FCSTD DOCUMENT  (FreeCAD 0.19R24291 (Git))
Label: Problem 09
License: All rights reserved
LicenseURL: http://en.wikipedia.org/wiki/All_rights_reserved
objects: Part::Part2DObjectPython×72, App::FeaturePython×42, Part::Mirroring×7
note: 79 computed .brp shape members not serialized (recipe doc carries the construction recipe); baked Part::Feature solids carry a one-line shape summary decoded from their .brp

FEATURE [Part::Part2DObjectPython] Line  # Draft 2D object (typed FeaturePython)
  Area = 0
  ChamferSize = 0
  Closed = false
  End = (-88.4143,-6.28415,0)
  FilletRadius = 0
  Length = 66.1082
  MakeFace = false
  Placement = pos=(-8.14865,-6.28415,0) rot=(0,0,1;0rad)
  Points = (2) [(-14.1575,6.21725e-15,0),(-80.2657,-8.88178e-16,0)]
  Start = (-22.3061,-6.28415,0)
  Subdivisions = 0
FEATURE [Part::Part2DObjectPython] Circle  # Draft 2D object (typed FeaturePython)
  Area = 0
  FirstAngle = 0
  LastAngle = 0
  MakeFace = false
  Placement = pos=(-1.0929,-49.8088,0) rot=(0,0,1;0rad)
  Radius = 30
FEATURE [Part::Part2DObjectPython] Line001  # Draft 2D object (typed FeaturePython)
  Area = 0
  ChamferSize = 0
  Closed = false
  End = (-31.0929,-6.28415,0)
  FilletRadius = 0
  Length = 43.5246
  MakeFace = false
  Placement = pos=(-31.0929,-49.8088,0) rot=(0,0,1;0rad)
  Points = (2) [(-7.10543e-15,1.13687e-13,0),(-3.55271e-15,43.5246,0)]
  Start = (-31.0929,-49.8088,0)
  Subdivisions = 0
FEATURE [Part::Part2DObjectPython] Line002  # Draft 2D object (typed FeaturePython)
  Area = 0
  ChamferSize = 0
  Closed = false
  End = (28.9071,-6.28415,0)
  FilletRadius = 0
  Length = 43.5246
  MakeFace = false
  Placement = pos=(28.9071,-49.8088,0) rot=(0,0,1;0rad)
  Points = (2) [(0,0,0),(3.55271e-15,43.5246,0)]
  Start = (28.9071,-49.8088,0)
  Subdivisions = 0
FEATURE [Part::Part2DObjectPython] Line003  # Draft 2D object (typed FeaturePython)
  Area = 0
  ChamferSize = 0
  Closed = false
  End = (-31.061,13.6349,0)
  FilletRadius = 0
  Length = 19.9191
  MakeFace = false
  Placement = pos=(-31.0929,-6.28415,0) rot=(0,0,-1;1.33891rad)
  Points = (2) [(0,0,0),(-19.3786,4.60874,0)]
  Start = (-31.0929,-6.28415,0)
  Subdivisions = 0
FEATURE [Part::Part2DObjectPython] Line004  # Draft 2D object (typed FeaturePython)
  Area = 0
  ChamferSize = 0
  Closed = false
  End = (28.9071,-6.28415,0)
  FilletRadius = 0
  Length = 60
  MakeFace = false
  Placement = pos=(-31.0929,-6.28415,0) rot=(0,0,1;0rad)
  Points = (2) [(0,0,0),(60,-8.88178e-15,0)]
  Start = (-31.0929,-6.28415,0)
  Subdivisions = 0
FEATURE [Part::Part2DObjectPython] Line005  # Draft 2D object (typed FeaturePython)
  Area = 0
  ChamferSize = 0
  Closed = false
  End = (28.9071,73.7165,0)
  FilletRadius = 0
  Length = 60
  MakeFace = false
  Points = (2) [(-31.0929,73.7165,0),(28.9071,73.7165,0)]
  Start = (-31.0929,73.7165,0)
  Subdivisions = 0
FEATURE [Part::Part2DObjectPython] Line006  # Draft 2D object (typed FeaturePython)
  Area = 0
  ChamferSize = 0
  Closed = false
  End = (28.9757,54.2966,0)
  FilletRadius = 0
  Length = 19.4201
  MakeFace = false
  Placement = pos=(28.9071,73.7165,0) rot=(0,0,1;0rad)
  Points = (2) [(0,0,0),(0.0686363,-19.4199,0)]
  Start = (28.9071,73.7165,0)
  Subdivisions = 0
FEATURE [Part::Part2DObjectPython] Line007  # Draft 2D object (typed FeaturePython)
  Area = 0
  ChamferSize = 0
  Closed = false
  End = (142.077,-19.8088,0)
  FilletRadius = 0
  Length = 143.169
  MakeFace = false
  Points = (2) [(-1.0929,-19.8088,0),(142.077,-19.8088,0)]
  Start = (-1.0929,-19.8088,0)
  Subdivisions = 0
FEATURE [Part::Part2DObjectPython] Line008  # Draft 2D object (typed FeaturePython)
  Area = 0
  ChamferSize = 0
  Closed = false
  End = (-1.0929,-79.8088,0)
  FilletRadius = 0
  Length = 203.169
  MakeFace = false
  Points = (2) [(202.077,-79.8088,0),(-1.0929,-79.8088,0)]
  Start = (202.077,-79.8088,0)
  Subdivisions = 0
FEATURE [Part::Part2DObjectPython] Line010  # Draft 2D object (typed FeaturePython)
  Area = 0
  ChamferSize = 0
  Closed = false
  End = (142.077,73.7158,0)
  FilletRadius = 0
  Length = 80
  MakeFace = false
  Placement = pos=(142.077,-19.8088,0) rot=(0,0,1;0rad)
  Points = (2) [(0,13.5246,0),(0,93.5246,0)]
  Start = (142.077,-6.28415,0)
  Subdivisions = 0
FEATURE [Part::Part2DObjectPython] Line011  # Draft 2D object (typed FeaturePython)
  Area = 0
  ChamferSize = 0
  Closed = false
  End = (202.077,73.7158,0)
  FilletRadius = 0
  Length = 80
  MakeFace = false
  Placement = pos=(202.077,-79.8088,0) rot=(0,0,1;0rad)
  Points = (2) [(0,73.5246,0),(-2.84217e-14,153.525,0)]
  Start = (202.077,-6.28415,0)
  Subdivisions = 0
FEATURE [Part::Part2DObjectPython] Line012  # Draft 2D object (typed FeaturePython)
  Area = 0
  ChamferSize = 0
  Closed = false
  End = (142.077,-6.28415,0)
  FilletRadius = 0
  Length = 73.5246
  MakeFace = false
  Placement = pos=(142.077,-19.8088,0) rot=(0,0,1;0rad)
  Points = (2) [(0,-60,0),(0,13.5246,0)]
  Start = (142.077,-79.8088,0)
  Subdivisions = 0
FEATURE [Part::Part2DObjectPython] Line013  # Draft 2D object (typed FeaturePython)
  Area = 0
  ChamferSize = 0
  Closed = false
  End = (202.077,-6.28415,0)
  FilletRadius = 0
  Length = 73.5246
  MakeFace = false
  Placement = pos=(202.077,-79.8088,0) rot=(0,0,1;0rad)
  Points = (2) [(0,0,0),(0,73.5246,0)]
  Start = (202.077,-79.8088,0)
  Subdivisions = 0
FEATURE [Part::Part2DObjectPython] Line014  # Draft 2D object (typed FeaturePython)
  Area = 0
  ChamferSize = 0
  Closed = false
  End = (202.077,73.7158,0)
  FilletRadius = 0
  Length = 60
  MakeFace = false
  Placement = pos=(142.077,73.7158,0) rot=(0,0,1;0rad)
  Points = (2) [(0,0,0),(60,1.42109e-14,0)]
  Start = (142.077,73.7158,0)
  Subdivisions = 0
FEATURE [Part::Part2DObjectPython] Line015  # Draft 2D object (typed FeaturePython)
  Area = 0
  ChamferSize = 0
  Closed = false
  End = (172.077,73.7158,0)
  FilletRadius = 0
  Length = 123.525
  MakeFace = false
  Placement = pos=(172.077,73.7158,0) rot=(0,0,1;0rad)
  Points = (2) [(0,-123.525,0),(0,0,0)]
  Start = (172.077,-49.8088,0)
  Subdivisions = 0
FEATURE [Part::Part2DObjectPython] Line016  # Draft 2D object (typed FeaturePython)
  Area = 0
  ChamferSize = 0
  Closed = false
  End = (142.077,33.7158,0)
  FilletRadius = 0
  Length = 60
  MakeFace = false
  Placement = pos=(202.077,33.7158,0) rot=(0,0,1;0rad)
  Points = (2) [(0,0,0),(-60,-7.10543e-15,0)]
  Start = (202.077,33.7158,0)
  Subdivisions = 0
FEATURE [Part::Part2DObjectPython] Polygon  # Draft 2D object (typed FeaturePython)
  Area = 0
  ChamferSize = 0
  DrawMode = 0
  FacesNumber = 4
  FilletRadius = 0
  MakeFace = false
  Placement = pos=(172.077,33.7158,0) rot=(0,0,1;0rad)
  Radius = 21.2132
FEATURE [Part::Part2DObjectPython] Line017  # Draft 2D object (typed FeaturePython)
  Area = 0
  ChamferSize = 0
  Closed = false
  End = (150.863,33.7158,0)
  FilletRadius = 0
  Length = 113.525
  MakeFace = false
  Placement = pos=(150.863,33.7158,0) rot=(0,0,1;0rad)
  Points = (2) [(0,-113.525,0),(0,0,0)]
  Start = (150.863,-79.8088,0)
  Subdivisions = 0
FEATURE [Part::Part2DObjectPython] Line018  # Draft 2D object (typed FeaturePython)
  Area = 0
  ChamferSize = 0
  Closed = false
  End = (193.29,33.7158,0)
  FilletRadius = 0
  Length = 113.525
  MakeFace = false
  Placement = pos=(193.29,33.7158,0) rot=(0,0,1;0rad)
  Points = (2) [(0,-113.525,0),(0,0,0)]
  Start = (193.29,-79.8088,0)
  Subdivisions = 0
FEATURE [Part::Part2DObjectPython] Line019  # Draft 2D object (typed FeaturePython)
  Area = 0
  ChamferSize = 0
  Closed = false
  End = (161.47,44.3224,0)
  FilletRadius = 0
  Length = 124.131
  MakeFace = false
  Placement = pos=(161.47,44.3224,0) rot=(0,0,1;0rad)
  Points = (2) [(0,-124.131,0),(0,2.84217e-14,0)]
  Start = (161.47,-79.8088,0)
  Subdivisions = 0
FEATURE [Part::Part2DObjectPython] Line020  # Draft 2D object (typed FeaturePython)
  Area = 0
  ChamferSize = 0
  Closed = false
  End = (182.683,44.3224,0)
  FilletRadius = 0
  Length = 124.131
  MakeFace = false
  Placement = pos=(182.683,44.3224,0) rot=(0,0,1;0rad)
  Points = (2) [(0,-124.131,0),(0,2.84217e-14,0)]
  Start = (182.683,-79.8088,0)
  Subdivisions = 0
FEATURE [App::FeaturePython] Text  # WARN: FeaturePython — macro-defined, semantics opaque (R4)
  Placement = pos=(174.82,55.4955,0) rot=(0,0,1;0rad)
  Text = 1''
FEATURE [App::FeaturePython] Text001  # WARN: FeaturePython — macro-defined, semantics opaque (R4)
  Placement = pos=(183.942,45.1583,0) rot=(0,0,1;0rad)
  Text = 2''
FEATURE [App::FeaturePython] Text002  # WARN: FeaturePython — macro-defined, semantics opaque (R4)
  Placement = pos=(193.671,34.517,0) rot=(0,0,1;0rad)
  Text = 3''
FEATURE [App::FeaturePython] Text003  # WARN: FeaturePython — macro-defined, semantics opaque (R4)
  Placement = pos=(183.942,20.8354,0) rot=(0,0,1;0rad)
  Text = 4''
FEATURE [App::FeaturePython] Text004  # WARN: FeaturePython — macro-defined, semantics opaque (R4)
  Placement = pos=(172.692,8.67401,0) rot=(0,0,1;0rad)
  Text = 5''
FEATURE [App::FeaturePython] Text005  # WARN: FeaturePython — macro-defined, semantics opaque (R4)
  Placement = pos=(156.274,19.0112,0) rot=(0,0,1;0rad)
  Text = 6''
FEATURE [App::FeaturePython] Text006  # WARN: FeaturePython — macro-defined, semantics opaque (R4)
  Placement = pos=(147.457,35.7332,0) rot=(0,0,1;0rad)
  Text = 7''
FEATURE [App::FeaturePython] Text007  # WARN: FeaturePython — macro-defined, semantics opaque (R4)
  Placement = pos=(158.099,43.9421,0) rot=(0,0,1;0rad)
  Text = 8''
FEATURE [Part::Part2DObjectPython] Line022  # Draft 2D object (typed FeaturePython)
  Area = 0
  ChamferSize = 0
  Closed = false
  End = (161.47,-39.2022,0)
  FilletRadius = 0
  Length = 212.563
  MakeFace = false
  Placement = pos=(161.47,-39.2022,0) rot=(0,0,1;0rad)
  Points = (2) [(-212.563,-7.10543e-15,0),(0,0,0)]
  Start = (-51.0929,-39.2022,0)
  Subdivisions = 0
FEATURE [Part::Part2DObjectPython] Line023  # Draft 2D object (typed FeaturePython)
  Area = 0
  ChamferSize = 0
  Closed = false
  End = (182.683,-60.4154,0)
  FilletRadius = 0
  Length = 233.776
  MakeFace = false
  Placement = pos=(182.683,-60.4154,0) rot=(0,0,1;0rad)
  Points = (2) [(-233.776,0,0),(0,0,0)]
  Start = (-51.0929,-60.4154,0)
  Subdivisions = 0
FEATURE [Part::Part2DObjectPython] Line025  # Draft 2D object (typed FeaturePython)
  Area = 0
  ChamferSize = 0
  Closed = false
  End = (-1.0929,73.7165,0)
  FilletRadius = 0
  Length = 153.525
  MakeFace = false
  Placement = pos=(-1.0929,73.7165,0) rot=(0,0,1;0rad)
  Points = (2) [(-1.82077e-14,-153.525,0),(0,0,0)]
  Start = (-1.0929,-79.8088,0)
  Subdivisions = 0
FEATURE [Part::Part2DObjectPython] Line026  # Draft 2D object (typed FeaturePython)
  Area = 0
  ChamferSize = 0
  Closed = false
  End = (-29.1553,73.7165,0)
  FilletRadius = 0
  Length = 134.132
  MakeFace = false
  Placement = pos=(-29.1553,-39.2022,0) rot=(0,0,1;0rad)
  Points = (2) [(-1.06581e-14,-21.2132,0),(3.55271e-15,112.919,0)]
  Start = (-29.1553,-60.4154,0)
  Subdivisions = 0
FEATURE [Part::Part2DObjectPython] Line027  # Draft 2D object (typed FeaturePython)
  Area = 0
  ChamferSize = 0
  Closed = false
  End = (-22.3061,73.7165,0)
  FilletRadius = 0
  Length = 144.739
  MakeFace = false
  Placement = pos=(-22.3061,-71.022,0) rot=(0,0,1;0rad)
  Points = (2) [(0,0,0),(1.77636e-14,144.739,0)]
  Start = (-22.3061,-71.022,0)
  Subdivisions = 0
FEATURE [Part::Part2DObjectPython] Line028  # Draft 2D object (typed FeaturePython)
  Area = 0
  ChamferSize = 0
  Closed = false
  End = (20.1203,73.7165,0)
  FilletRadius = 0
  Length = 144.739
  MakeFace = false
  Placement = pos=(20.1203,-71.022,0) rot=(0,0,1;0rad)
  Points = (2) [(0,0,0),(2.13163e-14,144.739,0)]
  Start = (20.1203,-71.022,0)
  Subdivisions = 0
FEATURE [Part::Part2DObjectPython] Line029  # Draft 2D object (typed FeaturePython)
  Area = 0
  ChamferSize = 0
  Closed = false
  End = (26.9695,73.7165,0)
  FilletRadius = 0
  Length = 134.132
  MakeFace = false
  Placement = pos=(26.9695,-60.4154,0) rot=(0,0,1;0rad)
  Points = (2) [(0,0,0),(2.13163e-14,134.132,0)]
  Start = (26.9695,-60.4154,0)
  Subdivisions = 0
FEATURE [Part::Part2DObjectPython] Line031  # Draft 2D object (typed FeaturePython)
  Area = 0
  ChamferSize = 0
  Closed = false
  End = (182.683,44.3224,0)
  FilletRadius = 0
  Length = 233.776
  MakeFace = false
  Placement = pos=(182.683,44.3224,0) rot=(0,0,1;0rad)
  Points = (2) [(-233.776,7.10543e-15,0),(0,0,0)]
  Start = (-51.0929,44.3224,0)
  Subdivisions = 0
FEATURE [Part::Part2DObjectPython] Line032  # Draft 2D object (typed FeaturePython)
  Area = 0
  ChamferSize = 0
  Closed = false
  End = (182.683,23.1092,0)
  FilletRadius = 0
  Length = 233.776
  MakeFace = false
  Placement = pos=(182.683,23.1092,0) rot=(0,0,1;0rad)
  Points = (2) [(-233.776,2.4869e-14,0),(0,0,0)]
  Start = (-51.0929,23.1092,0)
  Subdivisions = 0
FEATURE [Part::Part2DObjectPython] Line034  # Draft 2D object (typed FeaturePython)
  Area = 0
  ChamferSize = 0
  Closed = false
  End = (29.1711,55.03,0)
  FilletRadius = 0
  Length = 30.2642
  MakeFace = false
  Placement = pos=(-1.0929,54.929,0) rot=(0,0,1;0rad)
  Points = (2) [(0,0,0),(30.264,0.100964,0)]
  Start = (-1.0929,54.929,0)
  Subdivisions = 0
FEATURE [Part::Part2DObjectPython] Line035  # Draft 2D object (typed FeaturePython)
  Area = 0
  ChamferSize = 0
  Closed = false
  End = (29.2442,12.5661,0)
  FilletRadius = 0
  Length = 30.3372
  MakeFace = false
  Placement = pos=(-1.0929,12.5026,0) rot=(0,0,1;0rad)
  Points = (2) [(0,0,0),(30.3371,0.0634774,0)]
  Start = (-1.0929,12.5026,0)
  Subdivisions = 0
FEATURE [Part::Mirroring] mirror  label="Line034 (mirrored)"
  Base = (-1.0929,73.7165,0)
  Normal = (-1,1e-16,0)
  Source = -> Line034
FEATURE [Part::Mirroring] mirror001  label="Line035 (mirrored)"
  Base = (-1.0929,73.7165,0)
  Normal = (-1,1e-16,0)
  Source = -> Line035
FEATURE [Part::Part2DObjectPython] Line036  # Draft 2D object (typed FeaturePython)
  Area = 0
  ChamferSize = 0
  Closed = false
  End = (48.9071,23.1092,0)
  FilletRadius = 0
  Length = 31.8198
  MakeFace = false
  Placement = pos=(48.9071,54.929,0) rot=(0,0,1;0rad)
  Points = (2) [(0,0,0),(-7.10543e-15,-31.8198,0)]
  Start = (48.9071,54.929,0)
  Subdivisions = 0
FEATURE [Part::Part2DObjectPython] Line037  # Draft 2D object (typed FeaturePython)
  Area = 0
  ChamferSize = 0
  Closed = false
  End = (-51.0929,12.5026,0)
  FilletRadius = 0
  Length = 42.4264
  MakeFace = false
  Placement = pos=(-51.0929,54.929,0) rot=(0,0,1;0rad)
  Points = (2) [(0,0,0),(0,-42.4264,0)]
  Start = (-51.0929,54.929,0)
  Subdivisions = 0
FEATURE [App::FeaturePython] Text008  # WARN: FeaturePython — macro-defined, semantics opaque (R4)
  Placement = pos=(-34.6601,54.8874,0) rot=(0,0,1;0rad)
  Text = 1'
FEATURE [App::FeaturePython] Text009  # WARN: FeaturePython — macro-defined, semantics opaque (R4)
  Placement = pos=(30.4035,55.4955,0) rot=(0,0,1;0rad)
  Text = 1'
FEATURE [App::FeaturePython] Text010  # WARN: FeaturePython — macro-defined, semantics opaque (R4)
  Placement = pos=(-42.565,45.1583,0) rot=(0,0,1;0rad)
  Text = 2'(8')
FEATURE [App::FeaturePython] Text011  # WARN: FeaturePython — macro-defined, semantics opaque (R4)
  Placement = pos=(31.0116,44.8543,0) rot=(0,0,1;0rad)
  Text = 2'(8')
FEATURE [App::FeaturePython] Text012  # WARN: FeaturePython — macro-defined, semantics opaque (R4)
  Placement = pos=(-41.9569,24.4839,0) rot=(0,0,1;0rad)
  Text = 4'(6')
FEATURE [App::FeaturePython] Text013  # WARN: FeaturePython — macro-defined, semantics opaque (R4)
  Placement = pos=(30.7076,23.8758,0) rot=(0,0,1;0rad)
  Text = 4'(6')
FEATURE [App::FeaturePython] Text014  # WARN: FeaturePython — macro-defined, semantics opaque (R4)
  Placement = pos=(-36.1803,6.84981,0) rot=(0,0,1;0rad)
  Text = 5'
FEATURE [App::FeaturePython] Text015  # WARN: FeaturePython — macro-defined, semantics opaque (R4)
  Placement = pos=(31.9237,7.15383,0) rot=(0,0,1;0rad)
  Text = 5'
FEATURE [App::FeaturePython] Text016  # WARN: FeaturePython — macro-defined, semantics opaque (R4)
  Placement = pos=(-36.1803,74.6497,0) rot=(0,0,1;0rad)
  Text = p'
FEATURE [App::FeaturePython] Text017  # WARN: FeaturePython — macro-defined, semantics opaque (R4)
  Placement = pos=(30.4035,74.6497,0) rot=(0,0,1;0rad)
  Text = r'
FEATURE [App::FeaturePython] Text018  # WARN: FeaturePython — macro-defined, semantics opaque (R4)
  Placement = pos=(-35.5722,-5.00759,0) rot=(0,0,1;0rad)
  Text = i'
FEATURE [App::FeaturePython] Text019  # WARN: FeaturePython — macro-defined, semantics opaque (R4)
  Placement = pos=(30.7076,-5.9197,0) rot=(0,0,1;0rad)
  Text = k'
FEATURE [App::FeaturePython] Text020  # WARN: FeaturePython — macro-defined, semantics opaque (R4)
  Placement = pos=(-7.62939e-06,-5.00759,0) rot=(0,0,1;0rad)
  Text = j'(l')
FEATURE [App::FeaturePython] Text021  # WARN: FeaturePython — macro-defined, semantics opaque (R4)
  Placement = pos=(-3.64843,76.1699,0) rot=(0,0,1;0rad)
  Text = q'(s')
FEATURE [App::FeaturePython] Text022  # WARN: FeaturePython — macro-defined, semantics opaque (R4)
  Placement = pos=(-0.608087,-18.6892,0) rot=(0,0,1;0rad)
  Text = s(l)
FEATURE [App::FeaturePython] Text023  # WARN: FeaturePython — macro-defined, semantics opaque (R4)
  Placement = pos=(-38.6125,-56.3896,0) rot=(0,0,1;0rad)
  Text = p(i)
FEATURE [App::FeaturePython] Text024  # WARN: FeaturePython — macro-defined, semantics opaque (R4)
  Placement = pos=(30.7076,-56.3896,0) rot=(0,0,1;0rad)
  Text = r(k)
FEATURE [App::FeaturePython] Text025  # WARN: FeaturePython — macro-defined, semantics opaque (R4)
  Placement = pos=(-3.04037,-86.4891,0) rot=(0,0,1;0rad)
  Text = q(j)
FEATURE [Part::Part2DObjectPython] BSpline  # Draft 2D object (typed FeaturePython)
  Area = 0
  Closed = false
  MakeFace = false
  Parameterization = 1
  Points = (3) [(28.9071,54.929,0),(26.9695,44.3224,0),(20.1203,33.7158,0)]
FEATURE [Part::Mirroring] mirror002  label="BSpline (mirrored)"
  Base = (-1.0929,54.929,0)
  Normal = (-1,-4e-16,0)
  Source = -> BSpline
FEATURE [Part::Mirroring] mirror003  label="BSpline (mirrored) (mirrored)"
  Base = (-31.0288,33.7158,0)
  Normal = (0,-1,0)
  Source = -> mirror002
FEATURE [Part::Mirroring] mirror004  label="BSpline (mirrored)001"
  Base = (-31.0288,33.7158,0)
  Normal = (0,-1,0)
  Source = -> BSpline
FEATURE [Part::Part2DObjectPython] Line039  # Draft 2D object (typed FeaturePython)
  Area = 0
  ChamferSize = 0
  Closed = false
  End = (48.9071,-28.5956,0)
  FilletRadius = 0
  Length = 28.7868
  MakeFace = false
  Points = (2) [(20.1203,-28.5956,0),(48.9071,-28.5956,0)]
  Start = (20.1203,-28.5956,0)
  Subdivisions = 0
FEATURE [Part::Part2DObjectPython] Line040  # Draft 2D object (typed FeaturePython)
  Area = 0
  ChamferSize = 0
  Closed = false
  End = (-51.0929,-28.5956,0)
  FilletRadius = 0
  Length = 28.7868
  MakeFace = false
  Points = (2) [(-22.3061,-28.5956,0),(-51.0929,-28.5956,0)]
  Start = (-22.3061,-28.5956,0)
  Subdivisions = 0
FEATURE [Part::Mirroring] mirror005  label="Line039 (mirrored)"
  Base = (-1.0929,-49.8088,0)
  Normal = (0,1,0)
  Source = -> Line039
FEATURE [Part::Mirroring] mirror006  label="Line040 (mirrored)"
  Base = (-1.0929,-49.8088,0)
  Normal = (0,1,0)
  Source = -> Line040
FEATURE [Part::Part2DObjectPython] Line041  # Draft 2D object (typed FeaturePython)
  Area = 0
  ChamferSize = 0
  Closed = false
  End = (48.9071,-71.022,0)
  FilletRadius = 0
  Length = 42.4264
  MakeFace = false
  Placement = pos=(48.9071,-28.5956,0) rot=(0,0,1;0rad)
  Points = (2) [(0,0,0),(0,-42.4264,0)]
  Start = (48.9071,-28.5956,0)
  Subdivisions = 0
FEATURE [Part::Part2DObjectPython] Line042  # Draft 2D object (typed FeaturePython)
  Area = 0
  ChamferSize = 0
  Closed = false
  End = (-51.0929,-49.8088,0)
  FilletRadius = 0
  Length = 21.2132
  MakeFace = false
  Placement = pos=(-51.0929,-28.5956,0) rot=(0,0,1;0rad)
  Points = (2) [(0,0,0),(0,-21.2132,0)]
  Start = (-51.0929,-28.5956,0)
  Subdivisions = 0
FEATURE [Part::Part2DObjectPython] Line043  # Draft 2D object (typed FeaturePython)
  Area = 0
  ChamferSize = 0
  Closed = false
  End = (20.1203,-28.5956,0)
  FilletRadius = 0
  Length = 42.4264
  MakeFace = false
  Placement = pos=(-22.3061,-28.5956,0) rot=(0,0,1;0rad)
  Points = (2) [(0,0,0),(42.4264,7.10543e-15,0)]
  Start = (-22.3061,-28.5956,0)
  Subdivisions = 0
FEATURE [Part::Part2DObjectPython] Line044  # Draft 2D object (typed FeaturePython)
  Area = 0
  ChamferSize = 0
  Closed = false
  End = (20.1203,-71.022,0)
  FilletRadius = 0
  Length = 42.4264
  MakeFace = false
  Placement = pos=(-22.3061,-71.022,0) rot=(0,0,1;0rad)
  Points = (2) [(0,0,0),(42.4264,0,0)]
  Start = (-22.3061,-71.022,0)
  Subdivisions = 0
FEATURE [App::FeaturePython] Text026  # WARN: FeaturePython — macro-defined, semantics opaque (R4)
  Placement = pos=(-21.5361,28.4601,0) rot=(0,0,1;0rad)
  Text = 3'(7')
FEATURE [App::FeaturePython] Text027  # WARN: FeaturePython — macro-defined, semantics opaque (R4)
  Placement = pos=(7.49369,28.1698,0) rot=(0,0,1;0rad)
  Text = 3'(7')
FEATURE [Part::Part2DObjectPython] Line046  # Draft 2D object (typed FeaturePython)
  Area = 0
  ChamferSize = 0
  Closed = false
  End = (28.9071,-6.28415,0)
  FilletRadius = 0
  Length = 18.1974
  MakeFace = false
  Placement = pos=(28.9071,73.7165,0) rot=(0,0,1;0rad)
  Points = (2) [(0.0686363,-61.8034,0),(1.42109e-14,-80.0007,0)]
  Start = (28.9757,11.9131,0)
  Subdivisions = 0
FEATURE [Part::Part2DObjectPython] Line047  # Draft 2D object (typed FeaturePython)
  Area = 0
  ChamferSize = 0
  Closed = false
  End = (48.9071,54.929,0)
  FilletRadius = 0
  Length = 19.7362
  MakeFace = false
  Placement = pos=(-1.0929,54.929,0) rot=(0,0,1;0rad)
  Points = (2) [(30.264,0.100964,0),(50,-7.10543e-15,0)]
  Start = (29.1711,55.03,0)
  Subdivisions = 0
FEATURE [Part::Part2DObjectPython] Line048  # Draft 2D object (typed FeaturePython)
  Area = 0
  ChamferSize = 0
  Closed = false
  End = (48.9071,12.5026,0)
  FilletRadius = 0
  Length = 19.663
  MakeFace = false
  Placement = pos=(-1.0929,12.5026,0) rot=(0,0,1;0rad)
  Points = (2) [(30.3371,0.0634774,0),(50,-5.32907e-15,0)]
  Start = (29.2442,12.5661,0)
  Subdivisions = 0
FEATURE [Part::Part2DObjectPython] Line049  # Draft 2D object (typed FeaturePython)
  Area = 0
  ChamferSize = 0
  Closed = false
  End = (-31.3569,55.03,0)
  FilletRadius = 0
  Length = 19.7362
  MakeFace = false
  Placement = pos=(-51.0929,54.929,0) rot=(0,0,1;0rad)
  Points = (2) [(0,0,0),(19.736,0.100964,0)]
  Start = (-51.0929,54.929,0)
  Subdivisions = 0
FEATURE [Part::Part2DObjectPython] Line050  # Draft 2D object (typed FeaturePython)
  Area = 0
  ChamferSize = 0
  Closed = false
  End = (-31.43,12.5661,0)
  FilletRadius = 0
  Length = 19.663
  MakeFace = false
  Placement = pos=(-51.0929,12.5026,0) rot=(0,0,1;0rad)
  Points = (2) [(0,0,0),(19.6629,0.0634774,0)]
  Start = (-51.0929,12.5026,0)
  Subdivisions = 0
FEATURE [Part::Part2DObjectPython] Line051  # Draft 2D object (typed FeaturePython)
  Area = 0
  ChamferSize = 0
  Closed = true
  End = (-31.0929,-6.28415,0)
  FilletRadius = 0
  Length = 0
  MakeFace = false
  Placement = pos=(-31.0929,-49.8088,0) rot=(0,0,1;0rad)
  Points = (2) [(-3.55271e-15,43.5246,0),(-3.55271e-15,43.5246,0)]
  Start = (-31.0929,-6.28415,0)
  Subdivisions = 0
FEATURE [Part::Part2DObjectPython] Line052  # Draft 2D object (typed FeaturePython)
  Area = 0
  ChamferSize = 0
  Closed = false
  End = (28.9071,-6.28415,0)
  FilletRadius = 0
  Length = 60
  MakeFace = false
  Placement = pos=(-71.4481,-6.28415,0) rot=(0,0,1;0rad)
  Points = (2) [(40.3552,3.55271e-15,0),(100.355,1.77636e-15,0)]
  Start = (-31.0929,-6.28415,0)
  Subdivisions = 0
FEATURE [Part::Part2DObjectPython] Line053  # Draft 2D object (typed FeaturePython)
  Area = 0
  ChamferSize = 0
  Closed = false
  End = (142.077,-6.28415,0)
  FilletRadius = 0
  Length = 113.169
  MakeFace = false
  Placement = pos=(-71.4481,-6.28415,0) rot=(0,0,1;0rad)
  Points = (2) [(100.355,1.77636e-15,0),(213.525,5.32907e-15,0)]
  Start = (28.9071,-6.28415,0)
  Subdivisions = 0
FEATURE [Part::Part2DObjectPython] Line054  # Draft 2D object (typed FeaturePython)
  Area = 0
  ChamferSize = 0
  Closed = false
  End = (142.077,-6.28415,0)
  FilletRadius = 0
  Length = 0
  MakeFace = false
  Placement = pos=(142.077,-19.8088,0) rot=(0,0,1;0rad)
  Points = (2) [(0,13.5246,0),(0,13.5246,0)]
  Start = (142.077,-6.28415,0)
  Subdivisions = 0
FEATURE [Part::Part2DObjectPython] Line055  # Draft 2D object (typed FeaturePython)
  Area = 0
  ChamferSize = 0
  Closed = false
  End = (202.077,-6.28415,0)
  FilletRadius = 0
  Length = 60
  MakeFace = false
  Placement = pos=(-71.4481,-6.28415,0) rot=(0,0,1;0rad)
  Points = (2) [(213.525,5.32907e-15,0),(273.525,1.06581e-14,0)]
  Start = (142.077,-6.28415,0)
  Subdivisions = 0
FEATURE [Part::Part2DObjectPython] Line056  # Draft 2D object (typed FeaturePython)
  Area = 0
  ChamferSize = 0
  Closed = false
  End = (202.077,-6.28415,0)
  FilletRadius = 0
  Length = 51.2433
  MakeFace = false
  Placement = pos=(-71.4481,-6.28415,0) rot=(0,0,1;0rad)
  Points = (2) [(324.768,1.5099e-14,0),(273.525,1.06581e-14,0)]
  Start = (253.32,-6.28415,0)
  Subdivisions = 0
FEATURE [Part::Part2DObjectPython] Line058  # Draft 2D object (typed FeaturePython)
  Area = 0
  ChamferSize = 0
  Closed = false
  End = (172.077,-49.8088,0)
  FilletRadius = 0
  Length = 123.169
  MakeFace = false
  Placement = pos=(172.077,-49.8088,0) rot=(0,0,1;0rad)
  Points = (2) [(-123.169,2.13163e-14,0),(0,0,0)]
  Start = (48.9071,-49.8088,0)
  Subdivisions = 0
FEATURE [Part::Part2DObjectPython] Line059  # Draft 2D object (typed FeaturePython)
  Area = 0
  ChamferSize = 0
  Closed = false
  End = (28.9071,-49.8088,0)
  FilletRadius = 0
  Length = 60
  MakeFace = false
  Placement = pos=(172.077,-49.8088,0) rot=(0,0,1;0rad)
  Points = (2) [(-203.169,2.84217e-14,0),(-143.169,-7.81597e-14,0)]
  Start = (-31.0929,-49.8088,0)
  Subdivisions = 0
FEATURE [Part::Part2DObjectPython] Line060  # Draft 2D object (typed FeaturePython)
  Area = 0
  ChamferSize = 0
  Closed = false
  End = (-51.0929,-71.022,0)
  FilletRadius = 0
  Length = 21.2132
  MakeFace = false
  Placement = pos=(-51.0929,-28.5956,0) rot=(0,0,1;0rad)
  Points = (2) [(0,-21.2132,0),(0,-42.4264,0)]
  Start = (-51.0929,-49.8088,0)
  Subdivisions = 0
FEATURE [Part::Part2DObjectPython] Line061  # Draft 2D object (typed FeaturePython)
  Area = 0
  ChamferSize = 0
  Closed = false
  End = (-31.0929,-49.8088,0)
  FilletRadius = 0
  Length = 20
  MakeFace = false
  Placement = pos=(172.077,-49.8088,0) rot=(0,0,1;0rad)
  Points = (2) [(-223.169,2.84217e-14,0),(-203.169,2.84217e-14,0)]
  Start = (-51.0929,-49.8088,0)
  Subdivisions = 0
FEATURE [Part::Part2DObjectPython] Line062  # Draft 2D object (typed FeaturePython)
  Area = 0
  ChamferSize = 0
  Closed = false
  End = (48.9071,12.5026,0)
  FilletRadius = 0
  Length = 10.6066
  MakeFace = false
  Placement = pos=(48.9071,54.929,0) rot=(0,0,1;0rad)
  Points = (2) [(-7.10543e-15,-31.8198,0),(-7.10543e-15,-42.4264,0)]
  Start = (48.9071,23.1092,0)
  Subdivisions = 0
FEATURE [Part::Part2DObjectPython] Line063  # Draft 2D object (typed FeaturePython)
  Area = 0
  ChamferSize = 0
  Closed = false
  End = (20.1203,33.7158,0)
  FilletRadius = 0
  Length = 42.4264
  MakeFace = false
  Placement = pos=(142.077,33.7158,0) rot=(0,0,1;0rad)
  Points = (2) [(-164.383,2.13163e-14,0),(-121.956,2.13163e-14,0)]
  Start = (-22.3061,33.7158,0)
  Subdivisions = 0
FEATURE [Part::Part2DObjectPython] Line064  # Draft 2D object (typed FeaturePython)
  Area = 0
  ChamferSize = 0
  Closed = false
  End = (48.9071,33.7158,0)
  FilletRadius = 0
  Length = 28.7868
  MakeFace = false
  Placement = pos=(142.077,33.7158,0) rot=(0,0,1;0rad)
  Points = (2) [(-121.956,2.13163e-14,0),(-93.1694,2.84217e-14,0)]
  Start = (20.1203,33.7158,0)
  Subdivisions = 0
FEATURE [Part::Part2DObjectPython] Line065  # Draft 2D object (typed FeaturePython)
  Area = 0
  ChamferSize = 0
  Closed = false
  End = (-30.9646,73.7165,0)
  FilletRadius = 0
  Length = 20.9631
  MakeFace = false
  Placement = pos=(-31.0929,-6.28415,0) rot=(0,0,-1;1.33891rad)
  Points = (2) [(-57.4357,13.6597,0),(-77.83,18.51,0)]
  Start = (-30.9983,52.7535,0)
  Subdivisions = 0
FEATURE [Part::Part2DObjectPython] Line066  # Draft 2D object (typed FeaturePython)
  Area = 0
  ChamferSize = 0
  Closed = false
  End = (28.9757,54.2966,0)
  FilletRadius = 0
  Length = 0
  MakeFace = false
  Placement = pos=(28.9071,73.7165,0) rot=(0,0,1;0rad)
  Points = (2) [(0.0686363,-19.4199,0),(0.0686363,-19.4199,0)]
  Start = (28.9757,54.2966,0)
  Subdivisions = 0
FEATURE [Part::Part2DObjectPython] Line067  # Draft 2D object (typed FeaturePython)
  Area = 0
  ChamferSize = 0
  Closed = false
  End = (-30.9983,52.7535,0)
  FilletRadius = 0
  Length = 39.1186
  MakeFace = false
  Placement = pos=(-31.0929,-6.28415,0) rot=(0,0,-1;1.33891rad)
  Points = (2) [(-19.3786,4.60874,0),(-57.4357,13.6597,0)]
  Start = (-31.061,13.6349,0)
  Subdivisions = 0
FEATURE [Part::Part2DObjectPython] Line068  # Draft 2D object (typed FeaturePython)
  Area = 0
  ChamferSize = 0
  Closed = false
  End = (142.077,33.7158,0)
  FilletRadius = 0
  Length = 93.1694
  MakeFace = false
  Placement = pos=(142.077,33.7158,0) rot=(0,0,1;0rad)
  Points = (2) [(-93.1694,3.55271e-14,0),(0,0,0)]
  Start = (48.9071,33.7158,0)
  Subdivisions = 0
FEATURE [Part::Part2DObjectPython] Line069  # Draft 2D object (typed FeaturePython)
  Area = 0
  ChamferSize = 0
  Closed = false
  End = (-22.3061,33.7158,0)
  FilletRadius = 0
  Length = 28.7868
  MakeFace = false
  Placement = pos=(142.077,33.7158,0) rot=(0,0,1;0rad)
  Points = (2) [(-193.169,2.13163e-14,0),(-164.383,2.13163e-14,0)]
  Start = (-51.0929,33.7158,0)
  Subdivisions = 0
FEATURE [Part::Part2DObjectPython] Line070  # Draft 2D object (typed FeaturePython)
  Area = 0
  ChamferSize = 0
  Closed = false
  End = (28.9071,12.5026,0)
  FilletRadius = 0
  Length = 42.4264
  MakeFace = false
  Placement = pos=(28.9071,54.929,0) rot=(0,0,1;0rad)
  Points = (2) [(0,0,0),(0,-42.4264,0)]
  Start = (28.9071,54.929,0)
  Subdivisions = 0
FEATURE [App::FeaturePython] Dimension  # Draft dimension (typed FeaturePython)
  Diameter = false
  Dimline = (219.292,19.994,0)
  Direction = (0,0,0)
  Distance = 40
  End = (150.863,33.7158,0)
  Normal = (0,0,1)
  Start = (150.863,-6.28415,0)
FEATURE [App::FeaturePython] Dimension001  # Draft dimension (typed FeaturePython)
  Diameter = false
  Dimline = (232.535,-2.66679,0)
  Direction = (0,0,0)
  Distance = 80.0007
  End = (-1.0929,-6.28415,0)
  Normal = (0,0,1)
  Start = (-1.0929,73.7165,0)
FEATURE [Part::Part2DObjectPython] Line009  # Draft 2D object (typed FeaturePython)
  Area = 0
  ChamferSize = 0
  Closed = false
  End = (128.552,-6.28415,0)
  FilletRadius = 0
  Length = 125.763
  MakeFace = false
  Placement = pos=(128.552,-6.28415,0) rot=(0,0,1;0rad)
  Points = (2) [(88.9278,-88.9278,0),(0,1.77636e-15,0)]
  Start = (217.48,-95.212,0)
  Subdivisions = 0
FEATURE [App::FeaturePython] Dimension002  # Draft dimension (typed FeaturePython)
  Angle = 45
  Center = (128.552,-6.28415,0)
  Dimline = (135.708,-11.0699,0)
  FirstAngle = 315
  LastAngle = 360
  Normal = (0,0,1)
FEATURE [Part::Part2DObjectPython] Line071  # Draft 2D object (typed FeaturePython)
  Area = 0
  ChamferSize = 0
  Closed = false
  End = (48.9071,-49.8088,0)
  FilletRadius = 0
  Length = 20
  MakeFace = false
  Placement = pos=(172.077,-49.8088,0) rot=(0,0,1;0rad)
  Points = (2) [(-143.169,-7.81597e-14,0),(-123.169,2.13163e-14,0)]
  Start = (28.9071,-49.8088,0)
  Subdivisions = 0
FEATURE [App::FeaturePython] Dimension003  # Draft dimension (typed FeaturePython)
  Diameter = true
  Dimline = (-29.1553,-39.2022,0)
  Direction = (0,0,0)
  Distance = 60
  End = (-29.1553,-39.2022,0)
  LinkedGeometry = -> [Circle]
  Normal = (0,0,1)
  Start = (26.9695,-60.4154,0)
  Support = -> Circle
FEATURE [Part::Part2DObjectPython] Line072  # Draft 2D object (typed FeaturePython)
  Area = 0
  ChamferSize = 0
  Closed = false
  End = (193.29,-71.022,0)
  FilletRadius = 0
  Length = 144.383
  MakeFace = false
  Placement = pos=(48.9071,-71.022,0) rot=(0,0,1;0rad)
  Points = (2) [(0,0,0),(144.383,-4.26326e-14,0)]
  Start = (48.9071,-71.022,0)
  Subdivisions = 0
FEATURE [Part::Part2DObjectPython] Line073  # Draft 2D object (typed FeaturePython)
  Area = 0
  ChamferSize = 0
  Closed = false
  End = (150.863,-28.5956,0)
  FilletRadius = 0
  Length = 101.956
  MakeFace = false
  Placement = pos=(48.9071,-28.5956,0) rot=(0,0,1;0rad)
  Points = (2) [(0,0,0),(101.956,-3.55271e-15,0)]
  Start = (48.9071,-28.5956,0)
  Subdivisions = 0
FEATURE [Part::Part2DObjectPython] Line074  # Draft 2D object (typed FeaturePython)
  Area = 0
  ChamferSize = 0
  Closed = false
  End = (172.077,54.929,0)
  FilletRadius = 0
  Length = 123.169
  MakeFace = false
  Placement = pos=(48.9071,54.929,0) rot=(0,0,1;0rad)
  Points = (2) [(0,0,0),(123.169,-1.42109e-14,0)]
  Start = (48.9071,54.929,0)
  Subdivisions = 0
FEATURE [Part::Part2DObjectPython] Line075  # Draft 2D object (typed FeaturePython)
  Area = 0
  ChamferSize = 0
  Closed = false
  End = (172.077,12.5026,0)
  FilletRadius = 0
  Length = 123.169
  MakeFace = false
  Placement = pos=(48.9071,12.5026,0) rot=(0,0,1;0rad)
  Points = (2) [(0,0,0),(123.169,-1.24345e-14,0)]
  Start = (48.9071,12.5026,0)
  Subdivisions = 0
FEATURE [App::FeaturePython] Text028  # WARN: FeaturePython — macro-defined, semantics opaque (R4)
  Placement = pos=(-16.05,88.5211,0) rot=(0,0,1;0rad)
  Text = FRONT VIEW
FEATURE [App::FeaturePython] Text029  # WARN: FeaturePython — macro-defined, semantics opaque (R4)
  Placement = pos=(148.67,87.5726,0) rot=(0,0,1;0rad)
  Text = LEFT SIDE VIEW
FEATURE [App::FeaturePython] Text030  # WARN: FeaturePython — macro-defined, semantics opaque (R4)
  Placement = pos=(-16.6823,-110.661,0) rot=(0,0,1;0rad)
  Text = TOP VIEW
FEATURE [App::FeaturePython] Text031  # WARN: FeaturePython — macro-defined, semantics opaque (R4)
  Placement = pos=(53.5056,-116.668,0) rot=(0,0,1;0rad)
  Text = ALL DIMENSIONS ARE IN mm
FEATURE [App::FeaturePython] Text032  # WARN: FeaturePython — macro-defined, semantics opaque (R4)
  Placement = pos=(-89.7157,3.1574,0) rot=(0,0,1;0rad)
  Text = X
FEATURE [App::FeaturePython] Text033  # WARN: FeaturePython — macro-defined, semantics opaque (R4)
  Placement = pos=(243.519,2.84123,0) rot=(0,0,1;0rad)
  Text = Y
FEATURE [App::FeaturePython] Text034  # WARN: FeaturePython — macro-defined, semantics opaque (R4)
  Placement = pos=(-67.5843,2.20891,0) rot=(0,0,1;0rad)
  Text = VP
FEATURE [App::FeaturePython] Text035  # WARN: FeaturePython — macro-defined, semantics opaque (R4)
  Placement = pos=(-67.5843,-17.077,0) rot=(0,0,1;0rad)
  Text = HP
FEATURE [App::FeaturePython] Dimension004  # Draft dimension (typed FeaturePython)
  Diameter = false
  Dimline = (29.7935,-94.5366,0)
  Direction = (0,0,0)
  Distance = 100
  End = (48.9071,12.5026,0)
  Normal = (0,0,1)
  Start = (-51.0929,12.5026,0)
FEATURE [App::FeaturePython] Text036  # WARN: FeaturePython — macro-defined, semantics opaque (R4)
  Placement = pos=(-13.8368,-55.9649,0) rot=(0,0,1;0rad)
  Text = o(o1)
